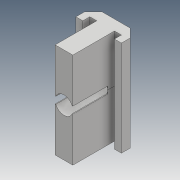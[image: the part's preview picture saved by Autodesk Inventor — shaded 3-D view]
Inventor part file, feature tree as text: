
AUTODESK INVENTOR PART (.ipt)
format: ipt  version: 2017 (Build 210142000, 142)  size: 135,680 bytes
history: native  units: mm
features: extrude x4, sketch x4, other x1, chamfer x1
ambient origin geometry x8: Origin, YZ Plane, XZ Plane, XY Plane, X Axis, Y Axis, Z Axis, Center Point
bodies: Body1 (feature_tree)
feature tree (10):
  other  "Sólido1"
  extrude  "Extrusión1"  Depth=20.0mm TaperAngle=0.0deg
  extrude  "Extrusión2"  Depth=10.0mm TaperAngle=0.0deg
  extrude  "Extrusión3"  Depth=4.0mm TaperAngle=0.0deg
  chamfer  "Chaflán1"  Distance=5.0mm Angle=45.0deg
  extrude  "Extrusión4"  Depth=4.0mm
  sketch  "Boceto1"  dims[d0=10.2mm d1=20.0mm d2=0.0mm]
  sketch  "Boceto2"  dims[d3=8.0mm d4=10.0mm d5=0.0mm]
  sketch  "Boceto3"  dims[d6=4.0mm d7=15.0mm d8=0.0mm d9=5.0mm d10=2.0mm d11=45.0deg]
  sketch  "Boceto4"  dims[d12=55.0mm d13=4.0mm d14=4.0mm d15=4.0mm d16=0.0mm]
